# Revit family: Domotics-DomesticRanges-GEWISS-SYSTEM_POWER-SOCKET-OUTLET_ITA_P11P17_16A
name_source: partatom
category: Apparecchi elettrici
revit_build: Autodesk Revit 2016 (Build: 20161004_0715(x64)
units: mm (PartAtom-declared; Revit-internal decimal feet)

## family parameters
Condiviso = Sì
Host = Superficie
Mantenere orientamento annotazione = Sì
Numero OmniClass = 23.80.50.14
Punto di calcolo locali = Sì
Quota connettore circolare = Usa diametro
Taglio con vuoti quando caricato = No
Tipo di parte = Normale
Titolo OmniClass = Plug Connectors

## types (4) — shared parameters
Carico apparente = 0 VA
Catalogue = DOMOTICS
Catalogue Range = SYSTEM - DOMESTIC RANGE
Characteristics = 2P+E - 16 A Dual amperage
Description. = Dual amperage socket-outlet
Description: = 2P+E - 16 A Dual amperage
Electrocod = 0131
For plug pins = Ã˜ 4 / 5 mm
IDF = 09b57737-3f5e-45a4-9267-f0fc22462c9d
IDT = 04ccb2e4-3fec-40e1-92c1-48c33f491795
Immagine tipo = GW20295.jpg
Larghezza presa = 23 mm  [stored 0.0754593 ft]
N. poli = 2
No. SYSTEM modules = 1
Produttore = GEWISS S.p.A.
Prospetto di default = 1219 mm
SEO = Socket outlet
Simbolo_ = SIMBOLO PRESE : PRESA
Standard = English
Standard: = English
Technical sheet = https://www.gewiss.com
Tipo_ = SYSTEM PRESE ITA P11-17 16A_BASE : GW20295 - PRESA 2P+T 16A BIV.ST.ITAL.CON SCH.RED
Type = P17-11
Typology = P17-11
URL = https://www.gewiss.com
Version file RFA = 19.4
Volt = 230 V
Voltage = 250 V ac
Voltage: = 250 V ac

## per-type parameters (varying)
| type | Colour | Descrizione | EAN code | Modello | Type: |
| GW20286 - 2P+E 16A dual amp orange socket-outlet | Orange | 2P+E 16A DUAL AMP ORANGE SOCKET-OUTLET | 8011564079458 | GW20286 | For allocated lines |
| GW20295 - 2P+E 16A dual amp red socket-outlet | Red | 2P+E 16A DUAL AMP RED SOCKET-OUTLET | 8011564044869 | GW20295 | For allocated lines |
| GW20203 - 16A 2P+E dual amp.ital.s.-outlet white | White | 16A 2P+E DUAL AMP.ITAL.S.-OUTLET SY/WT | 8011564000537 | GW20203 |  |
| GW20281 - 2P+E 16A dual amp green socket-outlet | Green | 2P+E 16A DUAL AMP GREEN SOCKET-OUTLET | 8011564079427 | GW20281 | For allocated lines |

note: [stored X ft] marks values corroborated as IEEE doubles in the binary element streams (Revit-internal decimal feet)

## geometry (parser evidence)
native form markers: Sweep x1
no freeform markers — native parametric forms only
